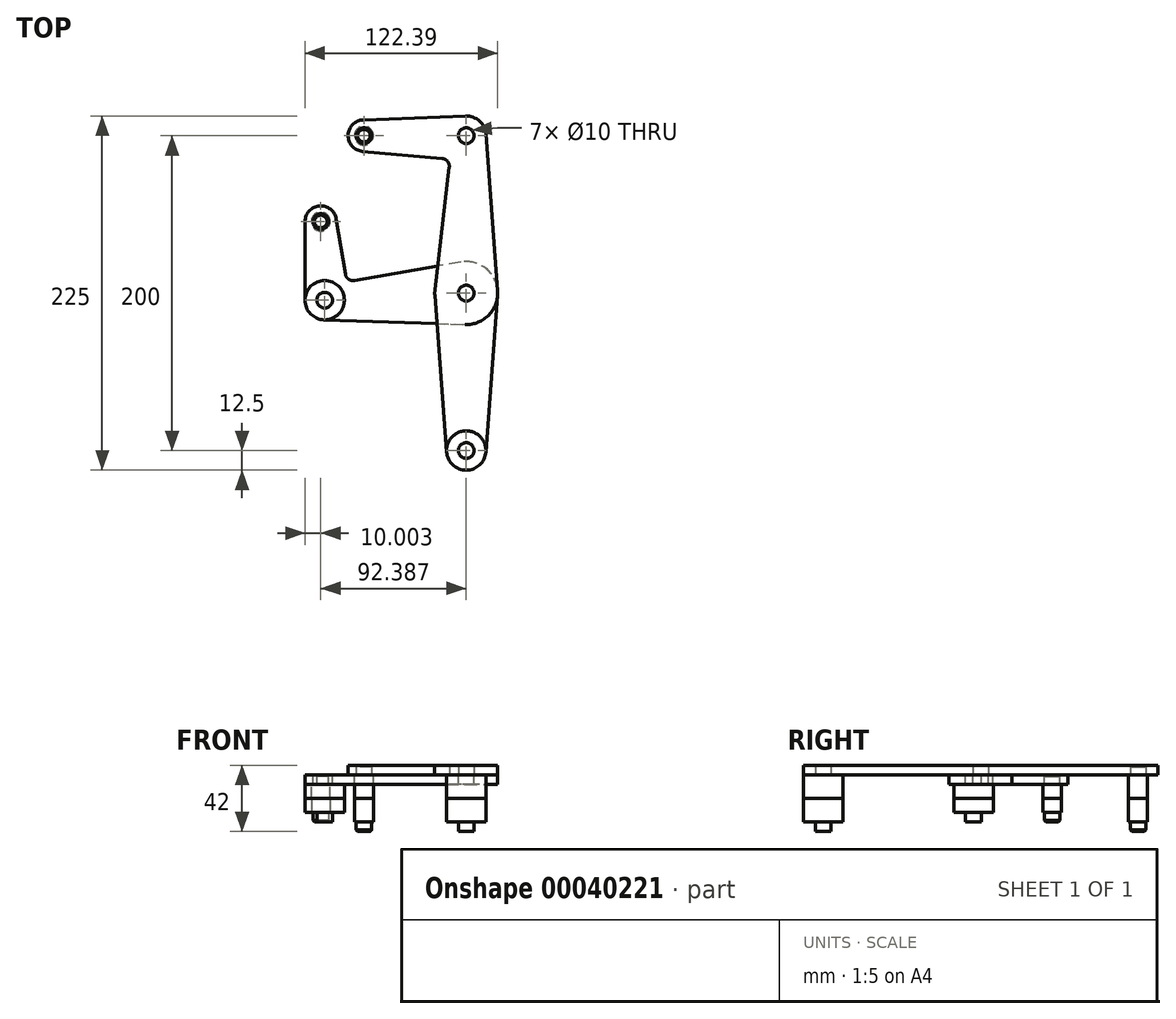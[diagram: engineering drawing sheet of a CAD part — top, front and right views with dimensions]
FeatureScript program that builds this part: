
annotation { "Feature Type Name" : "Feature", "Feature Type Description" : "" }
export const myFeature = defineFeature(function(context is Context, id is Id, definition is map)
    precondition{}
    {
        {
            var Q0;
            Q0=qCreatedBy(makeId("Top.planeOp"),FACE);
            cPlane(context, id + "F0", {"entities" : qUnion([Q0]), "cplaneType" : CPlaneType.OFFSET, "offset" : 15 * mm, "width" : 150 * mm, "height" : 150 * mm});
        }
        {
            var Q0;
            Q0=qCreatedBy(id+"F0.planeOp",FACE);
            var sketch = newSketch(context, id + "F1", { "sketchPlane" : qUnion([Q0])});
            skCircle(sketch, "E0", {"center": v(0, 0) * mm, "radius": 20 * mm});
            skLineSegment(sketch, "E1", {"start": v(0, -100) * mm, "end": v(0, 100) * mm, "construction": true});
            skLineSegment(sketch, "E2", {"start": v(0, 100) * mm, "end": v(-65, 100) * mm, "construction": true});
            skLineSegment(sketch, "E3", {"start": v(0, 0) * mm, "end": v(-89.89, -4.5) * mm, "construction": true});
            skLineSegment(sketch, "E4", {"start": v(-89.89, -4.5) * mm, "end": v(-92.39, 45.44) * mm, "construction": true});
            skCircle(sketch, "E5", {"center": v(0, 100) * mm, "radius": 12.5 * mm});
            skCircle(sketch, "E6", {"center": v(0, 100) * mm, "radius": 5 * mm});
            skCircle(sketch, "E7", {"center": v(-65, 100) * mm, "radius": 10 * mm});
            skCircle(sketch, "E8", {"center": v(-65, 100) * mm, "radius": 5 * mm});
            skCircle(sketch, "E9", {"center": v(-89.89, -4.5) * mm, "radius": 12.5 * mm});
            skCircle(sketch, "E10", {"center": v(-89.89, -4.5) * mm, "radius": 5 * mm});
            skCircle(sketch, "E11", {"center": v(-92.39, 45.44) * mm, "radius": 10 * mm});
            skCircle(sketch, "E12", {"center": v(-92.39, 45.44) * mm, "radius": 5 * mm});
            skCircle(sketch, "E13", {"center": v(0, -100) * mm, "radius": 12.5 * mm});
            skCircle(sketch, "E14", {"center": v(0, -100) * mm, "radius": 5 * mm});
            skLineSegment(sketch, "E15", {"start": v(-19.86, 2.33) * mm, "end": v(-10.78, 79.91) * mm});
            skLineSegment(sketch, "E16", {"start": v(-15.3, 85.47) * mm, "end": v(-65.9, 90.04) * mm});
            skLineSegment(sketch, "E17", {"start": v(-65.38, 110) * mm, "end": v(-0.48, 112.5) * mm});
            skLineSegment(sketch, "E18", {"start": v(12.46, 100.94) * mm, "end": v(19.94, 1.5) * mm});
            skLineSegment(sketch, "E19", {"start": v(19.94, -1.5) * mm, "end": v(12.46, -100.94) * mm});
            skLineSegment(sketch, "E20", {"start": v(-12.46, -100.94) * mm, "end": v(-19.94, -1.5) * mm});
            skLineSegment(sketch, "E21", {"start": v(-3.43, 19.7) * mm, "end": v(-71, 7.95) * mm});
            skLineSegment(sketch, "E22", {"start": v(-76.79, 12.07) * mm, "end": v(-82.52, 47.05) * mm});
            skLineSegment(sketch, "E23", {"start": v(-102.39, 45.44) * mm, "end": v(-102.39, -4.5) * mm});
            skLineSegment(sketch, "E24", {"start": v(-90.3, -17) * mm, "end": v(-0.67, -19.99) * mm});
            skPoint(sketch, "E25.visualSharp", {"position": v(-10.18, 85) * mm});
            skArc(sketch, "E25.filletArc", {"start": v(-10.78, 79.91) * mm, "mid": v(-11.86, 83.64) * mm, "end": v(-15.3, 85.47) * mm});
            skPoint(sketch, "E26.visualSharp", {"position": v(-75.97, 7.1) * mm});
            skArc(sketch, "E26.filletArc", {"start": v(-76.79, 12.07) * mm, "mid": v(-74.75, 8.8) * mm, "end": v(-71, 7.95) * mm});
            skCircle(sketch, "E27", {"center": v(0, 0) * mm, "radius": 5 * mm});
            skSolve(sketch);
        }
        {
            var Q0;
            {var subQ8=sQuery(id+"F1.wireOp",EDGE,"E16");Q0=makeQuery(id+"F1.imprint","IMPRINT",FACE,{"disambiguationData":[TD([[makeQuery(id+"F1.imprint","IMPRINT",EDGE,{"derivedFrom":subQ8}),-1.0]])]});}
            var Q1;
            Q1=makeQuery(id+"F1.imprint","IMPRINT",FACE,{"disambiguationData":[TD([[makeQuery(id+"F1.imprint","IMPRINT",EDGE,{"derivedFrom":sQuery(id+"F1.wireOp",EDGE,"E8")}),-1.0]])]});
            var Q2;
            Q2=makeQuery(id+"F1.imprint","IMPRINT",FACE,{"disambiguationData":[TD([[makeQuery(id+"F1.imprint","IMPRINT",EDGE,{"derivedFrom":sQuery(id+"F1.wireOp",EDGE,"E6")}),-1.0]])]});
            var Q3;
            Q3=makeQuery(id+"F1.imprint","IMPRINT",FACE,{"disambiguationData":[TD([[makeQuery(id+"F1.imprint","IMPRINT",EDGE,{"derivedFrom":sQuery(id+"F1.wireOp",EDGE,"E27")}),-1.0]])]});
            var Q4;
            {var subQ7=sQuery(id+"F1.wireOp",EDGE,"E19");Q4=makeQuery(id+"F1.imprint","IMPRINT",FACE,{"disambiguationData":[TD([[makeQuery(id+"F1.imprint","IMPRINT",EDGE,{"derivedFrom":subQ7}),-1.0]])]});}
            var Q5;
            Q5=makeQuery(id+"F1.imprint","IMPRINT",FACE,{"disambiguationData":[TD([[makeQuery(id+"F1.imprint","IMPRINT",EDGE,{"derivedFrom":sQuery(id+"F1.wireOp",EDGE,"E14")}),-1.0]])]});
            var Q6;
            {var subQ1=sQuery(id+"F1.wireOp",EDGE,"E20");var subQ3=sQuery(id+"F1.wireOp",EDGE,"E0");var subQ5=makeQuery(id+"F1.imprint","INTERSECT",VERTEX,{"derivedFrom":[subQ3,subQ1]});Q6=makeQuery(id+"F1.imprint","IMPRINT",FACE,{"disambiguationData":[TD([[makeQuery(id+"F1.imprint","IMPRINT",EDGE,{"disambiguationData":[TD([[subQ5,-1.0]])],"derivedFrom":subQ3}),-1.0]])]});}
            var Q7;
            {var subQ0=sQuery(id+"F1.wireOp",EDGE,"E15");var subQ3=sQuery(id+"F1.wireOp",EDGE,"E0");var subQ4=makeQuery(id+"F1.imprint","INTERSECT",VERTEX,{"derivedFrom":[subQ3,subQ0]});Q7=makeQuery(id+"F1.imprint","IMPRINT",FACE,{"disambiguationData":[TD([[makeQuery(id+"F1.imprint","IMPRINT",EDGE,{"disambiguationData":[TD([[subQ4,1.0]])],"derivedFrom":subQ3}),-1.0]])]});}
            extrude(context, id + "F2", {"entities" : qUnion([Q0, Q1, Q2, Q3, Q4, Q5, Q6, Q7]), "depth" : 6 * mm});
        }
        {
            var Q0;
            Q0=makeQuery(id+"F1.imprint","IMPRINT",FACE,{"disambiguationData":[TD([[makeQuery(id+"F1.imprint","IMPRINT",EDGE,{"derivedFrom":sQuery(id+"F1.wireOp",EDGE,"E27")}),-1.0]])]});
            var Q1;
            {var subQ1=sQuery(id+"F1.wireOp",EDGE,"E22");Q1=makeQuery(id+"F1.imprint","IMPRINT",FACE,{"disambiguationData":[TD([[makeQuery(id+"F1.imprint","IMPRINT",EDGE,{"derivedFrom":subQ1}),1.0]])]});}
            var Q2;
            {var subQ1=sQuery(id+"F1.wireOp",EDGE,"E20");var subQ3=sQuery(id+"F1.wireOp",EDGE,"E0");var subQ5=makeQuery(id+"F1.imprint","INTERSECT",VERTEX,{"derivedFrom":[subQ3,subQ1]});Q2=makeQuery(id+"F1.imprint","IMPRINT",FACE,{"disambiguationData":[TD([[makeQuery(id+"F1.imprint","IMPRINT",EDGE,{"disambiguationData":[TD([[subQ5,-1.0]])],"derivedFrom":subQ3}),-1.0]])]});}
            var Q3;
            {var subQ0=sQuery(id+"F1.wireOp",EDGE,"E15");var subQ3=sQuery(id+"F1.wireOp",EDGE,"E0");var subQ4=makeQuery(id+"F1.imprint","INTERSECT",VERTEX,{"derivedFrom":[subQ3,subQ0]});Q3=makeQuery(id+"F1.imprint","IMPRINT",FACE,{"disambiguationData":[TD([[makeQuery(id+"F1.imprint","IMPRINT",EDGE,{"disambiguationData":[TD([[subQ4,1.0]])],"derivedFrom":subQ3}),-1.0]])]});}
            var Q4;
            Q4=makeQuery(id+"F1.imprint","IMPRINT",FACE,{"disambiguationData":[TD([[makeQuery(id+"F1.imprint","IMPRINT",EDGE,{"derivedFrom":sQuery(id+"F1.wireOp",EDGE,"E10")}),-1.0]])]});
            var Q5;
            Q5=makeQuery(id+"F1.imprint","IMPRINT",FACE,{"disambiguationData":[TD([[makeQuery(id+"F1.imprint","IMPRINT",EDGE,{"derivedFrom":sQuery(id+"F1.wireOp",EDGE,"E12")}),-1.0]])]});
            extrude(context, id + "F3", {"entities" : qUnion([Q0, Q1, Q2, Q3, Q4, Q5]), "oppositeDirection" : true, "depth" : 6 * mm});
        }
        {
            var Q0;
            Q0=makeQuery(id+"F2.opExtrude","CAP_FACE",FACE,{"disambiguationData":[OSD([sQuery(id+"F1.wireOp",EDGE,"E0"),sQuery(id+"F1.wireOp",EDGE,"E5"),sQuery(id+"F1.wireOp",EDGE,"E6"),sQuery(id+"F1.wireOp",EDGE,"E7"),sQuery(id+"F1.wireOp",EDGE,"E8"),sQuery(id+"F1.wireOp",EDGE,"E13"),sQuery(id+"F1.wireOp",EDGE,"E14"),sQuery(id+"F1.wireOp",EDGE,"E15"),sQuery(id+"F1.wireOp",EDGE,"E16"),sQuery(id+"F1.wireOp",EDGE,"E17"),sQuery(id+"F1.wireOp",EDGE,"E18"),sQuery(id+"F1.wireOp",EDGE,"E19"),sQuery(id+"F1.wireOp",EDGE,"E20"),sQuery(id+"F1.wireOp",EDGE,"E25.filletArc"),sQuery(id+"F1.wireOp",EDGE,"E27")])],"isStart":false});
            var sketch = newSketch(context, id + "F4", { "sketchPlane" : qUnion([Q0])});
            skCircle(sketch, "E28", {"center": v(-65, 100) * mm, "radius": 6 * mm});
            skCircle(sketch, "E29", {"center": v(0, -100) * mm, "radius": 12.5 * mm});
            skSolve(sketch);
        }
        {
            var Q0;
            Q0=makeQuery(id+"F3.opExtrude","CAP_FACE",FACE,{"disambiguationData":[OSD([sQuery(id+"F1.wireOp",EDGE,"E0"),sQuery(id+"F1.wireOp",EDGE,"E9"),sQuery(id+"F1.wireOp",EDGE,"E10"),sQuery(id+"F1.wireOp",EDGE,"E11"),sQuery(id+"F1.wireOp",EDGE,"E12"),sQuery(id+"F1.wireOp",EDGE,"E21"),sQuery(id+"F1.wireOp",EDGE,"E22"),sQuery(id+"F1.wireOp",EDGE,"E23"),sQuery(id+"F1.wireOp",EDGE,"E24"),sQuery(id+"F1.wireOp",EDGE,"E26.filletArc"),sQuery(id+"F1.wireOp",EDGE,"E27")])],"isStart":true});
            var sketch = newSketch(context, id + "F5", { "sketchPlane" : qUnion([Q0])});
            skCircle(sketch, "E30", {"center": v(-92.39, 45.44) * mm, "radius": 6 * mm});
            skCircle(sketch, "E31", {"center": v(-89.89, -4.5) * mm, "radius": 12.5 * mm});
            skSolve(sketch);
        }
        {
            var Q0;
            Q0 = qSketchRegion(id + "F5", true);
            var Q1;
            Q1 = qSketchRegion(id + "F4", true);
            var Q2;
            Q2=qCreatedBy(makeId("Top.planeOp"),FACE);
            extrude(context, id + "F6", {"entities" : qUnion([Q0, Q1]), "endBound" : BoundingType.UP_TO_SURFACE, "oppositeDirection" : true, "endBoundEntityFace" : qUnion([Q2]), "depth" : 25 * mm});
        }
        {
            var Q0;
            Q0=makeQuery(id+"F2.opExtrude","SWEPT_BODY",BODY,{"disambiguationData":[OSD([sQuery(id+"F1.wireOp",EDGE,"E0"),sQuery(id+"F1.wireOp",EDGE,"E5"),sQuery(id+"F1.wireOp",EDGE,"E6"),sQuery(id+"F1.wireOp",EDGE,"E7"),sQuery(id+"F1.wireOp",EDGE,"E8"),sQuery(id+"F1.wireOp",EDGE,"E13"),sQuery(id+"F1.wireOp",EDGE,"E14"),sQuery(id+"F1.wireOp",EDGE,"E15"),sQuery(id+"F1.wireOp",EDGE,"E16"),sQuery(id+"F1.wireOp",EDGE,"E17"),sQuery(id+"F1.wireOp",EDGE,"E18"),sQuery(id+"F1.wireOp",EDGE,"E19"),sQuery(id+"F1.wireOp",EDGE,"E20"),sQuery(id+"F1.wireOp",EDGE,"E25.filletArc"),sQuery(id+"F1.wireOp",EDGE,"E27")])]});
            var Q1;
            Q1=makeQuery(id+"F3.opExtrude","SWEPT_BODY",BODY,{"disambiguationData":[OSD([sQuery(id+"F1.wireOp",EDGE,"E0"),sQuery(id+"F1.wireOp",EDGE,"E9"),sQuery(id+"F1.wireOp",EDGE,"E10"),sQuery(id+"F1.wireOp",EDGE,"E11"),sQuery(id+"F1.wireOp",EDGE,"E12"),sQuery(id+"F1.wireOp",EDGE,"E21"),sQuery(id+"F1.wireOp",EDGE,"E22"),sQuery(id+"F1.wireOp",EDGE,"E23"),sQuery(id+"F1.wireOp",EDGE,"E24"),sQuery(id+"F1.wireOp",EDGE,"E26.filletArc"),sQuery(id+"F1.wireOp",EDGE,"E27")])]});
            var Q2;
            Q2=makeQuery(id+"F6.opExtrude","SWEPT_BODY",BODY,{"disambiguationData":[OSD([sQuery(id+"F4.wireOp",EDGE,"E28")])]});
            var Q3;
            Q3=makeQuery(id+"F6.opExtrude","SWEPT_BODY",BODY,{"disambiguationData":[OSD([sQuery(id+"F5.wireOp",EDGE,"E30")])]});
            var Q4;
            Q4=makeQuery(id+"F6.opExtrude","SWEPT_BODY",BODY,{"disambiguationData":[OSD([sQuery(id+"F5.wireOp",EDGE,"E31")])]});
            var Q5;
            Q5=makeQuery(id+"F6.opExtrude","SWEPT_BODY",BODY,{"disambiguationData":[OSD([sQuery(id+"F4.wireOp",EDGE,"E29")])]});
            booleanBodies(context, id + "F7", {"operationType" : BooleanOperationType.SUBTRACTION, "tools" : qUnion([Q0, Q1]), "targets" : qUnion([Q2, Q3, Q4, Q5]), "keepTools" : true});
        }
        {
            var Q0;
            Q0=makeQuery(id+"F6.opExtrude","CAP_FACE",FACE,{"disambiguationData":[OSD([sQuery(id+"F4.wireOp",EDGE,"E28")])],"isStart":true});
            var Q1;
            Q1=makeQuery(id+"F6.opExtrude","CAP_FACE",FACE,{"disambiguationData":[OSD([sQuery(id+"F5.wireOp",EDGE,"E30")])],"isStart":true});
            var Q2;
            Q2=makeQuery(id+"F7.opBoolean","COPY",EDGE,{"derivedFrom":makeQuery(id+"F3.opExtrude","CAP_EDGE",EDGE,{"disambiguationData":[OSD([sQuery(id+"F1.wireOp",EDGE,"E10")])],"isStart":true})});
            var Q3;
            Q3=makeQuery(id+"F7.opBoolean","COPY",EDGE,{"derivedFrom":makeQuery(id+"F2.opExtrude","CAP_EDGE",EDGE,{"disambiguationData":[OSD([sQuery(id+"F1.wireOp",EDGE,"E14")])],"isStart":false})});
            chamfer(context, id + "F8", {"entities" : qUnion([Q0, Q1, Q2, Q3]), "width" : 1 * mm, "tangentPropagation" : true});
        }
        {
            var Q0;
            Q0=makeQuery(id+"F6.opExtrude","SWEPT_BODY",BODY,{"disambiguationData":[OSD([sQuery(id+"F5.wireOp",EDGE,"E30")])]});
            var Q1;
            Q1=makeQuery(id+"F6.opExtrude","SWEPT_BODY",BODY,{"disambiguationData":[OSD([sQuery(id+"F4.wireOp",EDGE,"E28")])]});
            var Q2;
            Q2=makeQuery(id+"F6.opExtrude","SWEPT_BODY",BODY,{"disambiguationData":[OSD([sQuery(id+"F5.wireOp",EDGE,"E31")])]});
            var Q3;
            Q3=makeQuery(id+"F6.opExtrude","SWEPT_BODY",BODY,{"disambiguationData":[OSD([sQuery(id+"F4.wireOp",EDGE,"E29")])]});
            var Q4;
            Q4=qCreatedBy(makeId("Top.planeOp"),FACE);
            mirror(context, id + "F9", {"entities" : qUnion([Q0, Q1, Q2, Q3]), "mirrorPlane" : qUnion([Q4])});
        }
    });
